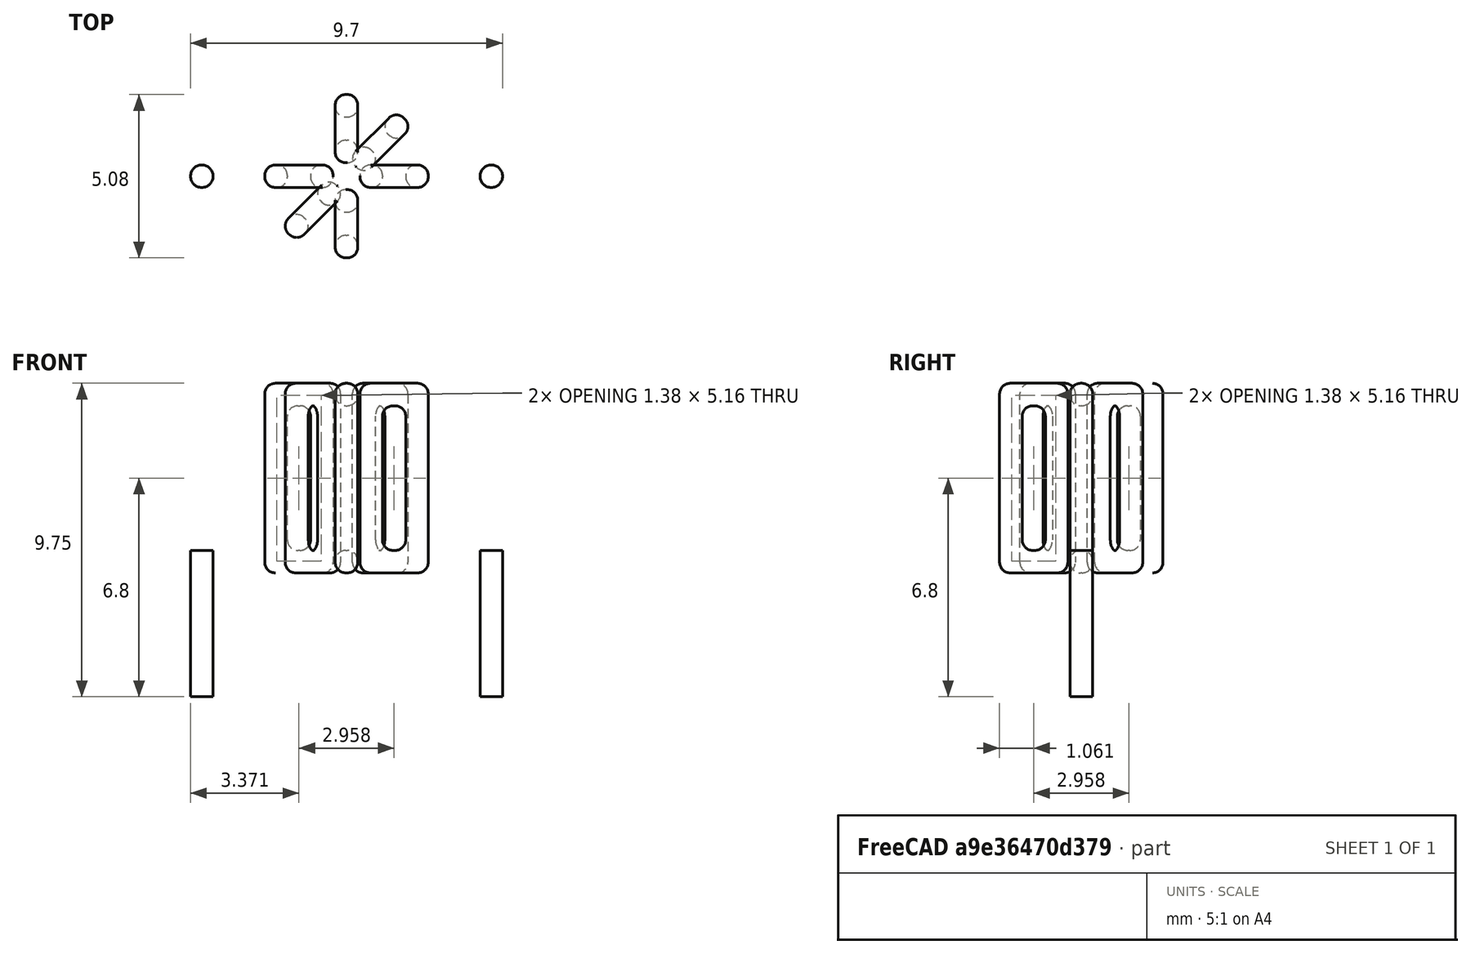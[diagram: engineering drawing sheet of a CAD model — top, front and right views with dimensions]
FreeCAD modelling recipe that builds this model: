
FCSTD DOCUMENT  (FreeCAD 0.16R6703 (Git))
Label: L_Toroid_Horizontal_D5.1mm_P9.00mm_Diameter6-5mm_Amidon-T20
License: All rights reserved
LicenseURL: http://en.wikipedia.org/wiki/All_rights_reserved
objects: Sketcher::SketchObject×6, PartDesign::Pad×6, PartDesign::Fillet×5, Spreadsheet::Sheet×1
note: 23 computed .brp shape members not serialized (recipe doc carries the construction recipe); baked Part::Feature solids carry a one-line shape summary decoded from their .brp

FEATURE [Spreadsheet::Sheet] Spreadsheet  label="dimensions"
  cells = A1=Wx; B1(Wx)=5.08; C1(WW)=2.2352; D1=5.08; A2=Wy; B2(Wy)=5.08; D2=5.08; A3=RM; B3(RMx)=9; C3(RMy)=0; A4=d_wire; B4(d_wire)=0.7; A5=H; B5(H)=4.5; A6=offsetx; B6(offsetx)=-1.96
FEATURE [Sketcher::SketchObject] Sketch
  Placement = pos=(0,0,1.2) rot=(0,0,1;0rad)
  expr: Placement.Base.z = 0.5 + Spreadsheet.d_wire
  expr: Constraints[0] = Spreadsheet.Wx / 2 - Spreadsheet.d_wire
  expr: Constraints[4] = Spreadsheet.WW / 2
  expr: Constraints[2] = Spreadsheet.RMy / 2
  expr: Constraints[1] = Spreadsheet.RMx / 2
  sketch-geometry (2):
    g0: Circle CenterX=4.5 CenterY=0 CenterZ=0 NormalX=0 NormalY=0 NormalZ=1 Radius=1.84
    g1: Circle CenterX=4.5 CenterY=0 CenterZ=0 NormalX=0 NormalY=0 NormalZ=1 Radius=1.1176
  constraints (5):
    c: Radius(g0) = 1.84
    c: DistanceX(g-1,g0) = 4.5
    c: DistanceY(g-1,g0) = 0
    c: Coincident(g1,g0)
    c: Radius(g1) = 1.1176
FEATURE [PartDesign::Pad] Pad
  Length = 4.5
  Length2 = 100
  Placement = pos=(0,0,1.2) rot=(0,0,1;0rad)
  Sketch = -> Sketch
  Type = 0
  expr: Length = Spreadsheet.H
FEATURE [Sketcher::SketchObject] Sketch001
  Placement = pos=(0,0,0.85) rot=(0,0,1;0rad)
  expr: Placement.Base.z = 0.5 + Spreadsheet.d_wire * 0.5
  expr: Constraints[4] = Spreadsheet.RMx
  expr: Constraints[2] = Spreadsheet.RMy
  expr: Constraints[1] = Spreadsheet.d_wire / 2
  sketch-geometry (2):
    g0: Circle CenterX=0 CenterY=0 CenterZ=0 NormalX=0 NormalY=0 NormalZ=1 Radius=0.35
    g1: Circle CenterX=9 CenterY=0 CenterZ=0 NormalX=0 NormalY=0 NormalZ=1 Radius=0.35
  constraints (5):
    c: Equal(g0,g1)
    c: Radius(g0) = 0.35
    c: DistanceY(g-1,g1) = 0
    c: Coincident(g0,g-1)
    c: DistanceX(g-1,g1) = 9
FEATURE [PartDesign::Pad] Pad001
  Length = 0.35
  Length2 = 4.2
  Placement = pos=(0,0,0.85) rot=(0,0,1;0rad)
  Reversed = true
  Sketch = -> Sketch001
  Type = 4
  expr: Length2 = 3.5 + Spreadsheet.d_wire
  expr: Length = Spreadsheet.d_wire / 2
FEATURE [PartDesign::Fillet] Fillet
  Base = -> Pad [Edge6,Edge3,Edge2]
  Placement = pos=(0,0,1.2) rot=(0,0,1;0rad)
  Radius = 0.5
FEATURE [Sketcher::SketchObject] Sketch003
  Placement = pos=(4.5,0,0) rot=(1,0,0;1.5708rad)
  expr: Placement.Base.x = Spreadsheet.RMx / 2
  expr: Constraints[49] = Spreadsheet.Wx - Spreadsheet.d_wire * 2
  expr: Constraints[44] = Spreadsheet.d_wire
  expr: Constraints[23] = Spreadsheet.H
  expr: Constraints[22] = Spreadsheet.Wx / 2 - Spreadsheet.d_wire
  expr: Placement.Base.y = Spreadsheet.RMy / 2
  expr: Constraints[21] = (Spreadsheet.Wx - Spreadsheet.WW) / 2 - Spreadsheet.d_wire
  expr: Constraints[19] = Spreadsheet.d_wire
  expr: Constraints[17] = Spreadsheet.d_wire
  expr: Constraints[18] = Spreadsheet.d_wire
  expr: Constraints[16] = Spreadsheet.d_wire
  sketch-geometry (16):
    g0: LineSegment StartX=-0.4176 StartY=0.5 StartZ=0 EndX=-2.54 EndY=0.5 EndZ=0
    g1: LineSegment StartX=-2.54 StartY=0.5 StartZ=0 EndX=-2.54 EndY=6.4 EndZ=0
    g2: LineSegment StartX=-2.54 StartY=6.4 StartZ=0 EndX=-0.4176 EndY=6.4 EndZ=0
    g3: LineSegment StartX=-0.4176 StartY=6.4 StartZ=0 EndX=-0.4176 EndY=0.5 EndZ=0
    g4: LineSegment StartX=-1.84 StartY=5.7 StartZ=0 EndX=-1.1176 EndY=5.7 EndZ=0
    g5: LineSegment StartX=-1.1176 StartY=5.7 StartZ=0 EndX=-1.1176 EndY=1.2 EndZ=0
    g6: LineSegment StartX=-1.1176 StartY=1.2 StartZ=0 EndX=-1.84 EndY=1.2 EndZ=0
    g7: LineSegment StartX=-1.84 StartY=1.2 StartZ=0 EndX=-1.84 EndY=5.7 EndZ=0
    g8: LineSegment StartX=0.4176 StartY=6.4 StartZ=0 EndX=2.54 EndY=6.4 EndZ=0
    g9: LineSegment StartX=2.54 StartY=6.4 StartZ=0 EndX=2.54 EndY=0.5 EndZ=0
    g10: LineSegment StartX=2.54 StartY=0.5 StartZ=0 EndX=0.4176 EndY=0.5 EndZ=0
    g11: LineSegment StartX=0.4176 StartY=0.5 StartZ=0 EndX=0.4176 EndY=6.4 EndZ=0
    g12: LineSegment StartX=1.1176 StartY=5.7 StartZ=0 EndX=1.84 EndY=5.7 EndZ=0
    g13: LineSegment StartX=1.84 StartY=5.7 StartZ=0 EndX=1.84 EndY=1.2 EndZ=0
    g14: LineSegment StartX=1.84 StartY=1.2 StartZ=0 EndX=1.1176 EndY=1.2 EndZ=0
    g15: LineSegment StartX=1.1176 StartY=1.2 StartZ=0 EndX=1.1176 EndY=5.7 EndZ=0
  constraints (50):
    c: Horizontal(g0)
    c: Coincident(g1,g0)
    c: Vertical(g1)
    c: Coincident(g2,g1)
    c: Horizontal(g2)
    c: Coincident(g3,g2)
    c: Coincident(g3,g0)
    c: Vertical(g3)
    c: Coincident(g4,g5)
    c: Coincident(g5,g6)
    c: Coincident(g6,g7)
    c: Coincident(g7,g4)
    c: Horizontal(g4)
    c: Horizontal(g6)
    c: Vertical(g5)
    c: Vertical(g7)
    c: DistanceX(g1,g4) = 0.7
    c: DistanceY(g4,g1) = 0.7
    c: DistanceX(g5,g0) = 0.7
    c: DistanceY(g0,g5) = 0.7
    c: DistanceY(g-1,g0) = 0.5
    c: DistanceX(g6,g6) = 0.7224
    c: DistanceX(g6,g-1) = 1.84
    c: DistanceY(g7,g7) = 4.5
    c: Coincident(g8,g9)
    c: Coincident(g9,g10)
    c: Coincident(g10,g11)
    c: Coincident(g11,g8)
    c: Horizontal(g8)
    c: Horizontal(g10)
    c: Vertical(g9)
    c: Vertical(g11)
    c: Coincident(g12,g13)
    c: Coincident(g13,g14)
    c: Coincident(g14,g15)
    c: Coincident(g15,g12)
    c: Horizontal(g12)
    c: Horizontal(g14)
    c: Vertical(g13)
    c: Vertical(g15)
    c: DistanceY(g8,g2) = 0
    c: DistanceY(g10,g0) = 0
    c: DistanceY(g14,g5) = 0
    c: DistanceY(g12,g4) = 0
    c: DistanceX(g8,g12) = 0.7
    c: Equal(g8,g2)
    c: Equal(g12,g4)
    c: Equal(g9,g1)
    c: Equal(g13,g7)
    c: DistanceX(g4,g12) = 3.68
FEATURE [PartDesign::Pad] Pad002
  Length = 0.7
  Length2 = 100
  Midplane = true
  Placement = pos=(4.5,0,0) rot=(1,0,0;1.5708rad)
  Sketch = -> Sketch003
  Type = 0
  expr: Length = Spreadsheet.d_wire
FEATURE [PartDesign::Fillet] Fillet001
  Base = -> Pad002 [Edge38,Edge41,Edge42,Edge43,Edge29,Edge32,Edge33,Edge34,Edge25,Edge35,Edge36,Edge13,Edge14,Edge15,Edge16,Edge17,Edge18,Edge19,Edge1,Edge2,Edge3,Edge4,Edge5,Edge6,Edge7,Edge37,Edge39,Edge40,Edge20,Edge23,Edge24,Edge21,Edge22,Edge8,Edge9,Edge10,Edge11,Edge12,Edge26,Edge27,+8 more]
  Placement = pos=(4.5,0,0) rot=(1,0,0;1.5708rad)
  Radius = 0.329
  expr: Radius = Spreadsheet.d_wire * 0.47
FEATURE [Sketcher::SketchObject] Sketch004
  Placement = pos=(4.5,0,0) rot=(0.862856,0.357407,0.357407;1.71777rad)
  expr: Placement.Base.x = Spreadsheet.RMx / 2
  expr: Constraints[49] = Spreadsheet.Wx - 2 * Spreadsheet.d_wire
  expr: Constraints[44] = Spreadsheet.d_wire
  expr: Constraints[23] = Spreadsheet.H
  expr: Constraints[22] = Spreadsheet.Wx / 2 - Spreadsheet.d_wire
  expr: Placement.Base.y = Spreadsheet.RMy / 2
  expr: Constraints[21] = (Spreadsheet.Wx - Spreadsheet.WW) / 2 - Spreadsheet.d_wire
  expr: Constraints[19] = Spreadsheet.d_wire
  expr: Constraints[17] = Spreadsheet.d_wire
  expr: Constraints[18] = Spreadsheet.d_wire
  expr: Constraints[16] = Spreadsheet.d_wire
  sketch-geometry (16):
    g0: LineSegment StartX=-0.4176 StartY=0.5 StartZ=0 EndX=-2.54 EndY=0.5 EndZ=0
    g1: LineSegment StartX=-2.54 StartY=0.5 StartZ=0 EndX=-2.54 EndY=6.4 EndZ=0
    g2: LineSegment StartX=-2.54 StartY=6.4 StartZ=0 EndX=-0.4176 EndY=6.4 EndZ=0
    g3: LineSegment StartX=-0.4176 StartY=6.4 StartZ=0 EndX=-0.4176 EndY=0.5 EndZ=0
    g4: LineSegment StartX=-1.84 StartY=5.7 StartZ=0 EndX=-1.1176 EndY=5.7 EndZ=0
    g5: LineSegment StartX=-1.1176 StartY=5.7 StartZ=0 EndX=-1.1176 EndY=1.2 EndZ=0
    g6: LineSegment StartX=-1.1176 StartY=1.2 StartZ=0 EndX=-1.84 EndY=1.2 EndZ=0
    g7: LineSegment StartX=-1.84 StartY=1.2 StartZ=0 EndX=-1.84 EndY=5.7 EndZ=0
    g8: LineSegment StartX=0.4176 StartY=6.4 StartZ=0 EndX=2.54 EndY=6.4 EndZ=0
    g9: LineSegment StartX=2.54 StartY=6.4 StartZ=0 EndX=2.54 EndY=0.5 EndZ=0
    g10: LineSegment StartX=2.54 StartY=0.5 StartZ=0 EndX=0.4176 EndY=0.5 EndZ=0
    g11: LineSegment StartX=0.4176 StartY=0.5 StartZ=0 EndX=0.4176 EndY=6.4 EndZ=0
    g12: LineSegment StartX=1.1176 StartY=5.7 StartZ=0 EndX=1.84 EndY=5.7 EndZ=0
    g13: LineSegment StartX=1.84 StartY=5.7 StartZ=0 EndX=1.84 EndY=1.2 EndZ=0
    g14: LineSegment StartX=1.84 StartY=1.2 StartZ=0 EndX=1.1176 EndY=1.2 EndZ=0
    g15: LineSegment StartX=1.1176 StartY=1.2 StartZ=0 EndX=1.1176 EndY=5.7 EndZ=0
  constraints (50):
    c: Horizontal(g0)
    c: Coincident(g1,g0)
    c: Vertical(g1)
    c: Coincident(g2,g1)
    c: Horizontal(g2)
    c: Coincident(g3,g2)
    c: Coincident(g3,g0)
    c: Vertical(g3)
    c: Coincident(g4,g5)
    c: Coincident(g5,g6)
    c: Coincident(g6,g7)
    c: Coincident(g7,g4)
    c: Horizontal(g4)
    c: Horizontal(g6)
    c: Vertical(g5)
    c: Vertical(g7)
    c: DistanceX(g1,g4) = 0.7
    c: DistanceY(g4,g1) = 0.7
    c: DistanceX(g5,g0) = 0.7
    c: DistanceY(g0,g5) = 0.7
    c: DistanceY(g-1,g0) = 0.5
    c: DistanceX(g6,g6) = 0.7224
    c: DistanceX(g6,g-1) = 1.84
    c: DistanceY(g7,g7) = 4.5
    c: Coincident(g8,g9)
    c: Coincident(g9,g10)
    c: Coincident(g10,g11)
    c: Coincident(g11,g8)
    c: Horizontal(g8)
    c: Horizontal(g10)
    c: Vertical(g9)
    c: Vertical(g11)
    c: Coincident(g12,g13)
    c: Coincident(g13,g14)
    c: Coincident(g14,g15)
    c: Coincident(g15,g12)
    c: Horizontal(g12)
    c: Horizontal(g14)
    c: Vertical(g13)
    c: Vertical(g15)
    c: DistanceY(g8,g2) = 0
    c: DistanceY(g10,g0) = 0
    c: DistanceY(g14,g5) = 0
    c: DistanceY(g12,g4) = 0
    c: DistanceX(g8,g12) = 0.7
    c: Equal(g8,g2)
    c: Equal(g12,g4)
    c: Equal(g9,g1)
    c: Equal(g13,g7)
    c: DistanceX(g4,g12) = 3.68
FEATURE [PartDesign::Pad] Pad003
  Length = 0.7
  Length2 = 100
  Midplane = true
  Placement = pos=(4.5,0,0) rot=(0.862856,0.357407,0.357407;1.71777rad)
  Sketch = -> Sketch004
  Type = 0
  expr: Length = Spreadsheet.d_wire
FEATURE [PartDesign::Fillet] Fillet002
  Base = -> Pad003 [Edge38,Edge41,Edge42,Edge43,Edge29,Edge32,Edge33,Edge34,Edge25,Edge35,Edge36,Edge13,Edge14,Edge15,Edge16,Edge17,Edge18,Edge19,Edge1,Edge2,Edge3,Edge4,Edge5,Edge6,Edge7,Edge37,Edge39,Edge40,Edge20,Edge23,Edge24,Edge21,Edge22,Edge8,Edge9,Edge10,Edge11,Edge12,Edge26,Edge27,+8 more]
  Placement = pos=(4.5,0,0) rot=(0.862856,0.357407,0.357407;1.71777rad)
  Radius = 0.329
  expr: Radius = Spreadsheet.d_wire * 0.47
FEATURE [Sketcher::SketchObject] Sketch005
  Placement = pos=(4.5,0,0) rot=(0.862856,-0.357407,-0.357407;1.71777rad)
  expr: Placement.Base.x = Spreadsheet.RMx / 2
  expr: Constraints[49] = Spreadsheet.Wx - 2 * Spreadsheet.d_wire
  expr: Constraints[44] = Spreadsheet.d_wire
  expr: Constraints[23] = Spreadsheet.H
  expr: Constraints[22] = Spreadsheet.Wx / 2 - Spreadsheet.d_wire
  expr: Placement.Base.y = Spreadsheet.RMy / 2
  expr: Constraints[21] = (Spreadsheet.Wx - Spreadsheet.WW) / 2 - Spreadsheet.d_wire
  expr: Constraints[19] = Spreadsheet.d_wire
  expr: Constraints[17] = Spreadsheet.d_wire
  expr: Constraints[18] = Spreadsheet.d_wire
  expr: Constraints[16] = Spreadsheet.d_wire
  sketch-geometry (16):
    g0: LineSegment StartX=-0.4176 StartY=0.5 StartZ=0 EndX=-2.54 EndY=0.5 EndZ=0
    g1: LineSegment StartX=-2.54 StartY=0.5 StartZ=0 EndX=-2.54 EndY=6.4 EndZ=0
    g2: LineSegment StartX=-2.54 StartY=6.4 StartZ=0 EndX=-0.4176 EndY=6.4 EndZ=0
    g3: LineSegment StartX=-0.4176 StartY=6.4 StartZ=0 EndX=-0.4176 EndY=0.5 EndZ=0
    g4: LineSegment StartX=-1.84 StartY=5.7 StartZ=0 EndX=-1.1176 EndY=5.7 EndZ=0
    g5: LineSegment StartX=-1.1176 StartY=5.7 StartZ=0 EndX=-1.1176 EndY=1.2 EndZ=0
    g6: LineSegment StartX=-1.1176 StartY=1.2 StartZ=0 EndX=-1.84 EndY=1.2 EndZ=0
    g7: LineSegment StartX=-1.84 StartY=1.2 StartZ=0 EndX=-1.84 EndY=5.7 EndZ=0
    g8: LineSegment StartX=0.4176 StartY=6.4 StartZ=0 EndX=2.54 EndY=6.4 EndZ=0
    g9: LineSegment StartX=2.54 StartY=6.4 StartZ=0 EndX=2.54 EndY=0.5 EndZ=0
    g10: LineSegment StartX=2.54 StartY=0.5 StartZ=0 EndX=0.4176 EndY=0.5 EndZ=0
    g11: LineSegment StartX=0.4176 StartY=0.5 StartZ=0 EndX=0.4176 EndY=6.4 EndZ=0
    g12: LineSegment StartX=1.1176 StartY=5.7 StartZ=0 EndX=1.84 EndY=5.7 EndZ=0
    g13: LineSegment StartX=1.84 StartY=5.7 StartZ=0 EndX=1.84 EndY=1.2 EndZ=0
    g14: LineSegment StartX=1.84 StartY=1.2 StartZ=0 EndX=1.1176 EndY=1.2 EndZ=0
    g15: LineSegment StartX=1.1176 StartY=1.2 StartZ=0 EndX=1.1176 EndY=5.7 EndZ=0
  constraints (50):
    c: Horizontal(g0)
    c: Coincident(g1,g0)
    c: Vertical(g1)
    c: Coincident(g2,g1)
    c: Horizontal(g2)
    c: Coincident(g3,g2)
    c: Coincident(g3,g0)
    c: Vertical(g3)
    c: Coincident(g4,g5)
    c: Coincident(g5,g6)
    c: Coincident(g6,g7)
    c: Coincident(g7,g4)
    c: Horizontal(g4)
    c: Horizontal(g6)
    c: Vertical(g5)
    c: Vertical(g7)
    c: DistanceX(g1,g4) = 0.7
    c: DistanceY(g4,g1) = 0.7
    c: DistanceX(g5,g0) = 0.7
    c: DistanceY(g0,g5) = 0.7
    c: DistanceY(g-1,g0) = 0.5
    c: DistanceX(g6,g6) = 0.7224
    c: DistanceX(g6,g-1) = 1.84
    c: DistanceY(g7,g7) = 4.5
    c: Coincident(g8,g9)
    c: Coincident(g9,g10)
    c: Coincident(g10,g11)
    c: Coincident(g11,g8)
    c: Horizontal(g8)
    c: Horizontal(g10)
    c: Vertical(g9)
    c: Vertical(g11)
    c: Coincident(g12,g13)
    c: Coincident(g13,g14)
    c: Coincident(g14,g15)
    c: Coincident(g15,g12)
    c: Horizontal(g12)
    c: Horizontal(g14)
    c: Vertical(g13)
    c: Vertical(g15)
    c: DistanceY(g8,g2) = 0
    c: DistanceY(g10,g0) = 0
    c: DistanceY(g14,g5) = 0
    c: DistanceY(g12,g4) = 0
    c: DistanceX(g8,g12) = 0.7
    c: Equal(g8,g2)
    c: Equal(g12,g4)
    c: Equal(g9,g1)
    c: Equal(g13,g7)
    c: DistanceX(g4,g12) = 3.68
FEATURE [PartDesign::Pad] Pad004
  Length = 0.7
  Length2 = 100
  Midplane = true
  Placement = pos=(4.5,0,0) rot=(0.862856,-0.357407,-0.357407;1.71777rad)
  Sketch = -> Sketch005
  Type = 0
  expr: Length = Spreadsheet.d_wire
FEATURE [PartDesign::Fillet] Fillet003
  Base = -> Pad004 [Edge38,Edge41,Edge42,Edge43,Edge29,Edge32,Edge33,Edge34,Edge25,Edge35,Edge36,Edge13,Edge14,Edge15,Edge16,Edge17,Edge18,Edge19,Edge1,Edge2,Edge3,Edge4,Edge5,Edge6,Edge7,Edge37,Edge39,Edge40,Edge20,Edge23,Edge24,Edge21,Edge22,Edge8,Edge9,Edge10,Edge11,Edge12,Edge26,Edge27,+8 more]
  Placement = pos=(4.5,0,0) rot=(0.862856,-0.357407,-0.357407;1.71777rad)
  Radius = 0.329
  expr: Radius = Spreadsheet.d_wire * 0.47
FEATURE [Sketcher::SketchObject] Sketch006
  Placement = pos=(4.5,0,0) rot=(0.57735,0.57735,0.57735;2.0944rad)
  expr: Placement.Base.x = Spreadsheet.RMx / 2
  expr: Constraints[49] = Spreadsheet.Wx - Spreadsheet.d_wire * 2
  expr: Constraints[44] = Spreadsheet.d_wire
  expr: Constraints[23] = Spreadsheet.H
  expr: Constraints[22] = Spreadsheet.Wx / 2 - Spreadsheet.d_wire
  expr: Placement.Base.y = Spreadsheet.RMy / 2
  expr: Constraints[21] = (Spreadsheet.Wx - Spreadsheet.WW) / 2 - Spreadsheet.d_wire
  expr: Constraints[19] = Spreadsheet.d_wire
  expr: Constraints[17] = Spreadsheet.d_wire
  expr: Constraints[18] = Spreadsheet.d_wire
  expr: Constraints[16] = Spreadsheet.d_wire
  sketch-geometry (16):
    g0: LineSegment StartX=-0.4176 StartY=0.5 StartZ=0 EndX=-2.54 EndY=0.5 EndZ=0
    g1: LineSegment StartX=-2.54 StartY=0.5 StartZ=0 EndX=-2.54 EndY=6.4 EndZ=0
    g2: LineSegment StartX=-2.54 StartY=6.4 StartZ=0 EndX=-0.4176 EndY=6.4 EndZ=0
    g3: LineSegment StartX=-0.4176 StartY=6.4 StartZ=0 EndX=-0.4176 EndY=0.5 EndZ=0
    g4: LineSegment StartX=-1.84 StartY=5.7 StartZ=0 EndX=-1.1176 EndY=5.7 EndZ=0
    g5: LineSegment StartX=-1.1176 StartY=5.7 StartZ=0 EndX=-1.1176 EndY=1.2 EndZ=0
    g6: LineSegment StartX=-1.1176 StartY=1.2 StartZ=0 EndX=-1.84 EndY=1.2 EndZ=0
    g7: LineSegment StartX=-1.84 StartY=1.2 StartZ=0 EndX=-1.84 EndY=5.7 EndZ=0
    g8: LineSegment StartX=0.4176 StartY=6.4 StartZ=0 EndX=2.54 EndY=6.4 EndZ=0
    g9: LineSegment StartX=2.54 StartY=6.4 StartZ=0 EndX=2.54 EndY=0.5 EndZ=0
    g10: LineSegment StartX=2.54 StartY=0.5 StartZ=0 EndX=0.4176 EndY=0.5 EndZ=0
    g11: LineSegment StartX=0.4176 StartY=0.5 StartZ=0 EndX=0.4176 EndY=6.4 EndZ=0
    g12: LineSegment StartX=1.1176 StartY=5.7 StartZ=0 EndX=1.84 EndY=5.7 EndZ=0
    g13: LineSegment StartX=1.84 StartY=5.7 StartZ=0 EndX=1.84 EndY=1.2 EndZ=0
    g14: LineSegment StartX=1.84 StartY=1.2 StartZ=0 EndX=1.1176 EndY=1.2 EndZ=0
    g15: LineSegment StartX=1.1176 StartY=1.2 StartZ=0 EndX=1.1176 EndY=5.7 EndZ=0
  constraints (50):
    c: Horizontal(g0)
    c: Coincident(g1,g0)
    c: Vertical(g1)
    c: Coincident(g2,g1)
    c: Horizontal(g2)
    c: Coincident(g3,g2)
    c: Coincident(g3,g0)
    c: Vertical(g3)
    c: Coincident(g4,g5)
    c: Coincident(g5,g6)
    c: Coincident(g6,g7)
    c: Coincident(g7,g4)
    c: Horizontal(g4)
    c: Horizontal(g6)
    c: Vertical(g5)
    c: Vertical(g7)
    c: DistanceX(g1,g4) = 0.7
    c: DistanceY(g4,g1) = 0.7
    c: DistanceX(g5,g0) = 0.7
    c: DistanceY(g0,g5) = 0.7
    c: DistanceY(g-1,g0) = 0.5
    c: DistanceX(g6,g6) = 0.7224
    c: DistanceX(g6,g-1) = 1.84
    c: DistanceY(g7,g7) = 4.5
    c: Coincident(g8,g9)
    c: Coincident(g9,g10)
    c: Coincident(g10,g11)
    c: Coincident(g11,g8)
    c: Horizontal(g8)
    c: Horizontal(g10)
    c: Vertical(g9)
    c: Vertical(g11)
    c: Coincident(g12,g13)
    c: Coincident(g13,g14)
    c: Coincident(g14,g15)
    c: Coincident(g15,g12)
    c: Horizontal(g12)
    c: Horizontal(g14)
    c: Vertical(g13)
    c: Vertical(g15)
    c: DistanceY(g8,g2) = 0
    c: DistanceY(g10,g0) = 0
    c: DistanceY(g14,g5) = 0
    c: DistanceY(g12,g4) = 0
    c: DistanceX(g8,g12) = 0.7
    c: Equal(g8,g2)
    c: Equal(g12,g4)
    c: Equal(g9,g1)
    c: Equal(g13,g7)
    c: DistanceX(g4,g12) = 3.68
FEATURE [PartDesign::Pad] Pad005
  Length = 0.7
  Length2 = 100
  Midplane = true
  Placement = pos=(4.5,0,0) rot=(0.57735,0.57735,0.57735;2.0944rad)
  Sketch = -> Sketch006
  Type = 0
  expr: Length = Spreadsheet.d_wire
FEATURE [PartDesign::Fillet] Fillet004
  Base = -> Pad005 [Edge38,Edge41,Edge42,Edge43,Edge29,Edge32,Edge33,Edge34,Edge25,Edge35,Edge36,Edge13,Edge14,Edge15,Edge16,Edge17,Edge18,Edge19,Edge1,Edge2,Edge3,Edge4,Edge5,Edge6,Edge7,Edge37,Edge39,Edge40,Edge20,Edge23,Edge24,Edge21,Edge22,Edge8,Edge9,Edge10,Edge11,Edge12,Edge26,Edge27,+8 more]
  Placement = pos=(4.5,0,0) rot=(0.57735,0.57735,0.57735;2.0944rad)
  Radius = 0.329
  expr: Radius = Spreadsheet.d_wire * 0.47
